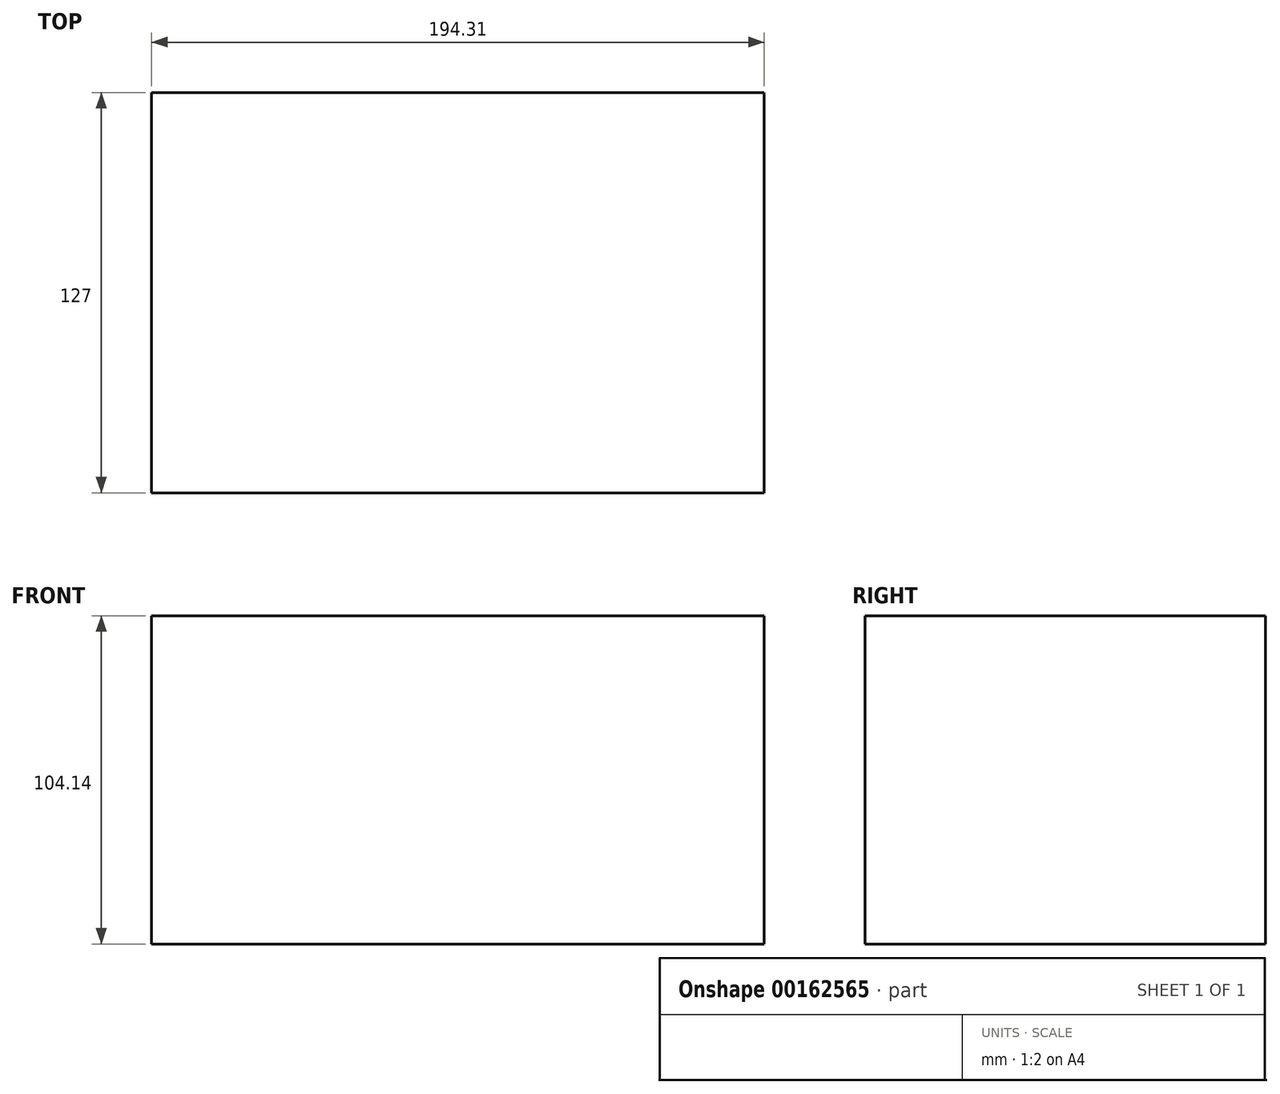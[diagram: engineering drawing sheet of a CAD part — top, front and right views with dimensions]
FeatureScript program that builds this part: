
annotation { "Feature Type Name" : "Feature", "Feature Type Description" : "" }
export const myFeature = defineFeature(function(context is Context, id is Id, definition is map)
    precondition{}
    {
        {
            var Q0;
            Q0=qCreatedBy(makeId("Top.planeOp"),FACE);
            var sketch = newSketch(context, id + "F0", { "sketchPlane" : qUnion([Q0])});
            skLineSegment(sketch, "E0.bottom", {"start": v(-40.96, 0) * mm, "end": v(35.24, 0) * mm});
            skLineSegment(sketch, "E0.top", {"start": v(-40.96, 127) * mm, "end": v(35.24, 127) * mm});
            skLineSegment(sketch, "E0.left", {"start": v(-40.96, 0) * mm, "end": v(-40.96, 127) * mm});
            skLineSegment(sketch, "E0.right", {"start": v(35.24, 0) * mm, "end": v(35.24, 127) * mm});
            skSolve(sketch);
        }
        {
            var Q0;
            Q0=makeQuery(id+"F0.imprint","IMPRINT",FACE,{"disambiguationData":[TD([[makeQuery(id+"F0.imprint","IMPRINT",EDGE,{"derivedFrom":sQuery(id+"F0.wireOp",EDGE,"E0.bottom")}),1.0]])]});
            extrude(context, id + "F1", {"entities" : qUnion([Q0]), "depth" : 50.8 * mm});
        }
        {
            var Q0;
            Q0=makeQuery(id+"F1.opExtrude","CAP_FACE",FACE,{"disambiguationData":[OSD([sQuery(id+"F0.wireOp",EDGE,"E0.bottom"),sQuery(id+"F0.wireOp",EDGE,"E0.top"),sQuery(id+"F0.wireOp",EDGE,"E0.left"),sQuery(id+"F0.wireOp",EDGE,"E0.right")])],"isStart":false});
            extrude(context, id + "F2", {"entities" : qUnion([Q0]), "operationType" : NewBodyOperationType.ADD, "depth" : 53.34 * mm});
        }
        {
            var Q0;
            {var subQ0=sQuery(id+"F0.wireOp",EDGE,"E0.right");Q0=makeQuery(id+"F2.boolean.opBoolean","MERGE",FACE,{"derivedFrom":[makeQuery(id+"F1.opExtrude","SWEPT_FACE",FACE,{"disambiguationData":[OSD([subQ0])]}),makeQuery(id+"F2.opExtrude","SWEPT_FACE",FACE,{"disambiguationData":[OSD([subQ0])]})]});}
            extrude(context, id + "F3", {"entities" : qUnion([Q0]), "operationType" : NewBodyOperationType.ADD, "depth" : 118.1 * mm});
        }
    });
